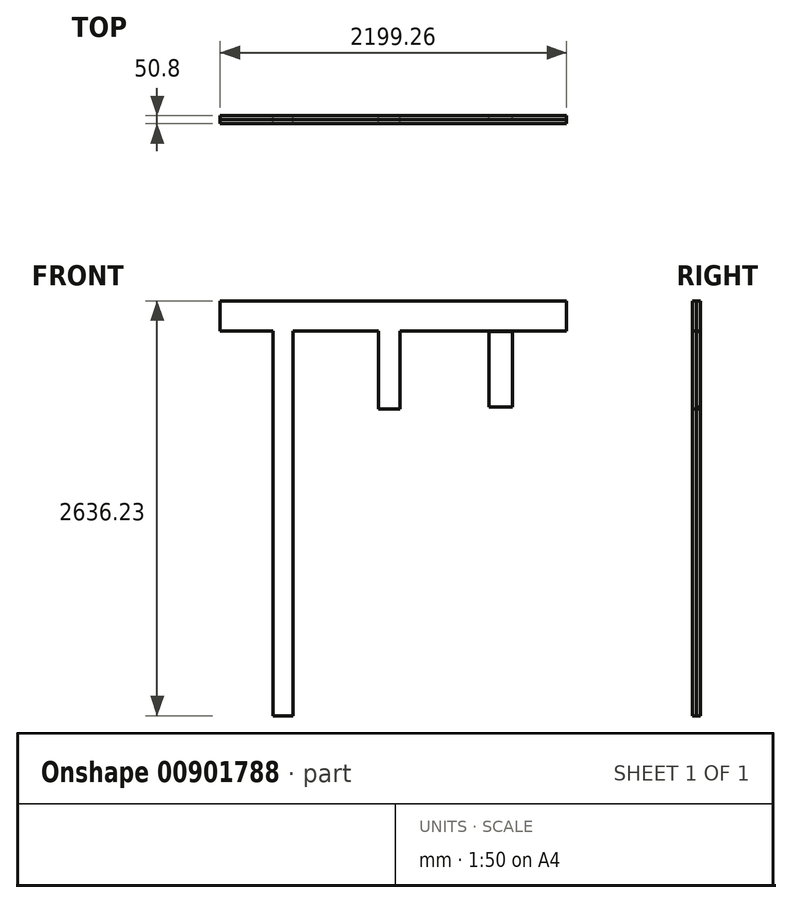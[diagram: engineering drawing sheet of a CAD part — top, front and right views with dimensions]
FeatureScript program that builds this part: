
annotation { "Feature Type Name" : "Feature", "Feature Type Description" : "" }
export const myFeature = defineFeature(function(context is Context, id is Id, definition is map)
    precondition{}
    {
        {
            var Q0;
            Q0=qCreatedBy(makeId("Front.planeOp"),FACE);
            var sketch = newSketch(context, id + "F0", { "sketchPlane" : qUnion([Q0])});
            skLineSegment(sketch, "E0.bottom", {"start": v(-1099.63, 96.23) * mm, "end": v(1099.63, 96.23) * mm});
            skLineSegment(sketch, "E0.top", {"start": v(-1099.63, -96.23) * mm, "end": v(1099.63, -96.23) * mm});
            skLineSegment(sketch, "E0.left", {"start": v(-1099.63, 96.23) * mm, "end": v(-1099.63, -96.23) * mm});
            skLineSegment(sketch, "E0.right", {"start": v(1099.63, 96.23) * mm, "end": v(1099.63, -96.23) * mm});
            skPoint(sketch, "E0.middle", {"position": v(0, 0) * mm});
            skLineSegment(sketch, "E1.bottom", {"start": v(-637.27, -2540) * mm, "end": v(-764.27, -2540) * mm});
            skLineSegment(sketch, "E1.top", {"start": v(-637.27, -2032) * mm, "end": v(-764.27, -2032) * mm});
            skLineSegment(sketch, "E1.left", {"start": v(-764.27, -2540) * mm, "end": v(-764.27, -2032) * mm});
            skLineSegment(sketch, "E1.right", {"start": v(-637.27, -2540) * mm, "end": v(-637.27, -2032) * mm});
            skPoint(sketch, "E1.middle", {"position": v(-700.77, -2286) * mm});
            skLineSegment(sketch, "E2.bottom", {"start": v(755.2, -578.3) * mm, "end": v(607.48, -578.3) * mm});
            skLineSegment(sketch, "E2.top", {"start": v(755.2, -97.78) * mm, "end": v(607.48, -97.78) * mm});
            skLineSegment(sketch, "E2.left", {"start": v(755.2, -578.3) * mm, "end": v(755.2, -97.78) * mm});
            skLineSegment(sketch, "E2.right", {"start": v(607.48, -578.3) * mm, "end": v(607.48, -97.78) * mm});
            skPoint(sketch, "E2.middle", {"position": v(681.34, -338.04) * mm});
            skLineSegment(sketch, "E3.bottom", {"start": v(-92.98, -96.23) * mm, "end": v(43.09, -96.23) * mm});
            skLineSegment(sketch, "E3.top", {"start": v(-92.98, -591.91) * mm, "end": v(43.09, -591.91) * mm});
            skLineSegment(sketch, "E3.left", {"start": v(-92.98, -96.23) * mm, "end": v(-92.98, -591.91) * mm});
            skLineSegment(sketch, "E3.right", {"start": v(43.09, -96.23) * mm, "end": v(43.09, -591.91) * mm});
            skLineSegment(sketch, "E4.top", {"start": v(-637.27, -96.23) * mm, "end": v(-764.27, -96.23) * mm});
            skLineSegment(sketch, "E4.left", {"start": v(-637.27, -2032) * mm, "end": v(-637.27, -96.23) * mm});
            skLineSegment(sketch, "E4.right", {"start": v(-764.27, -2032) * mm, "end": v(-764.27, -96.23) * mm});
            skSolve(sketch);
        }
        {
            var Q0;
            Q0=makeQuery(id+"F0.imprint","IMPRINT",FACE,{"disambiguationData":[TD([[makeQuery(id+"F0.imprint","IMPRINT",EDGE,{"derivedFrom":sQuery(id+"F0.wireOp",EDGE,"E1.top")}),-1.0]])]});
            var Q1;
            Q1=makeQuery(id+"F0.imprint","IMPRINT",FACE,{"disambiguationData":[TD([[makeQuery(id+"F0.imprint","IMPRINT",EDGE,{"derivedFrom":sQuery(id+"F0.wireOp",EDGE,"E1.bottom")}),-1.0]])]});
            var Q2;
            Q2=makeQuery(id+"F0.imprint","IMPRINT",FACE,{"disambiguationData":[TD([[makeQuery(id+"F0.imprint","IMPRINT",EDGE,{"derivedFrom":sQuery(id+"F0.wireOp",EDGE,"E3.top")}),1.0]])]});
            var Q3;
            Q3=makeQuery(id+"F0.imprint","IMPRINT",FACE,{"disambiguationData":[TD([[makeQuery(id+"F0.imprint","IMPRINT",EDGE,{"derivedFrom":sQuery(id+"F0.wireOp",EDGE,"E2.bottom")}),-1.0]])]});
            var Q4;
            Q4=makeQuery(id+"F0.imprint","IMPRINT",FACE,{"disambiguationData":[TD([[makeQuery(id+"F0.imprint","IMPRINT",EDGE,{"derivedFrom":sQuery(id+"F0.wireOp",EDGE,"E0.bottom")}),-1.0]])]});
            extrude(context, id + "F1", {"entities" : qUnion([Q0, Q1, Q2, Q3, Q4]), "depth" : 25.4 * mm, "offsetDistance" : 25.4 * mm});
        }
        {
            var Q0;
            {var subQ0=makeQuery(id+"F0.imprint","IMPRINT",EDGE,{"derivedFrom":sQuery(id+"F0.wireOp",EDGE,"E1.top")});Q0=qUnion([makeQuery(id+"F0.imprint","IMPRINT",FACE,{"disambiguationData":[TD([[makeQuery(id+"F0.imprint","IMPRINT",EDGE,{"derivedFrom":sQuery(id+"F0.wireOp",EDGE,"E2.bottom")}),-1.0]])]}),makeQuery(id+"F0.imprint","IMPRINT",FACE,{"disambiguationData":[TD([[makeQuery(id+"F0.imprint","IMPRINT",EDGE,{"derivedFrom":sQuery(id+"F0.wireOp",EDGE,"E0.bottom")}),-1.0]])]}),makeQuery(id+"F0.imprint","IMPRINT",FACE,{"disambiguationData":[TD([[subQ0,-1.0]])]}),makeQuery(id+"F0.imprint","IMPRINT",FACE,{"disambiguationData":[TD([[makeQuery(id+"F0.imprint","IMPRINT",EDGE,{"derivedFrom":sQuery(id+"F0.wireOp",EDGE,"E3.top")}),1.0]])]}),makeQuery(id+"F0.imprint","IMPRINT",FACE,{"disambiguationData":[TD([[makeQuery(id+"F0.imprint","IMPRINT",EDGE,{"derivedFrom":sQuery(id+"F0.wireOp",EDGE,"E1.bottom")}),-1.0]])]})]);}
            extrude(context, id + "F2", {"entities" : qUnion([Q0]), "depth" : 25.4 * mm, "offsetDistance" : 25.4 * mm});
        }
        {
            var Q0;
            Q0=makeQuery(id+"F1.opExtrude","CAP_FACE",FACE,{"disambiguationData":[OSD([sQuery(id+"F0.wireOp",EDGE,"E0.bottom"),sQuery(id+"F0.wireOp",EDGE,"E0.top"),sQuery(id+"F0.wireOp",EDGE,"E0.left"),sQuery(id+"F0.wireOp",EDGE,"E0.right"),sQuery(id+"F0.wireOp",EDGE,"E1.bottom"),sQuery(id+"F0.wireOp",EDGE,"E1.left"),sQuery(id+"F0.wireOp",EDGE,"E1.right"),sQuery(id+"F0.wireOp",EDGE,"E3.top"),sQuery(id+"F0.wireOp",EDGE,"E3.left"),sQuery(id+"F0.wireOp",EDGE,"E3.right"),sQuery(id+"F0.wireOp",EDGE,"E4.left"),sQuery(id+"F0.wireOp",EDGE,"E4.right")])],"isStart":false});
            extrude(context, id + "F3", {"entities" : qUnion([Q0]), "depth" : 25.4 * mm, "offsetDistance" : 25.4 * mm});
        }
    });
